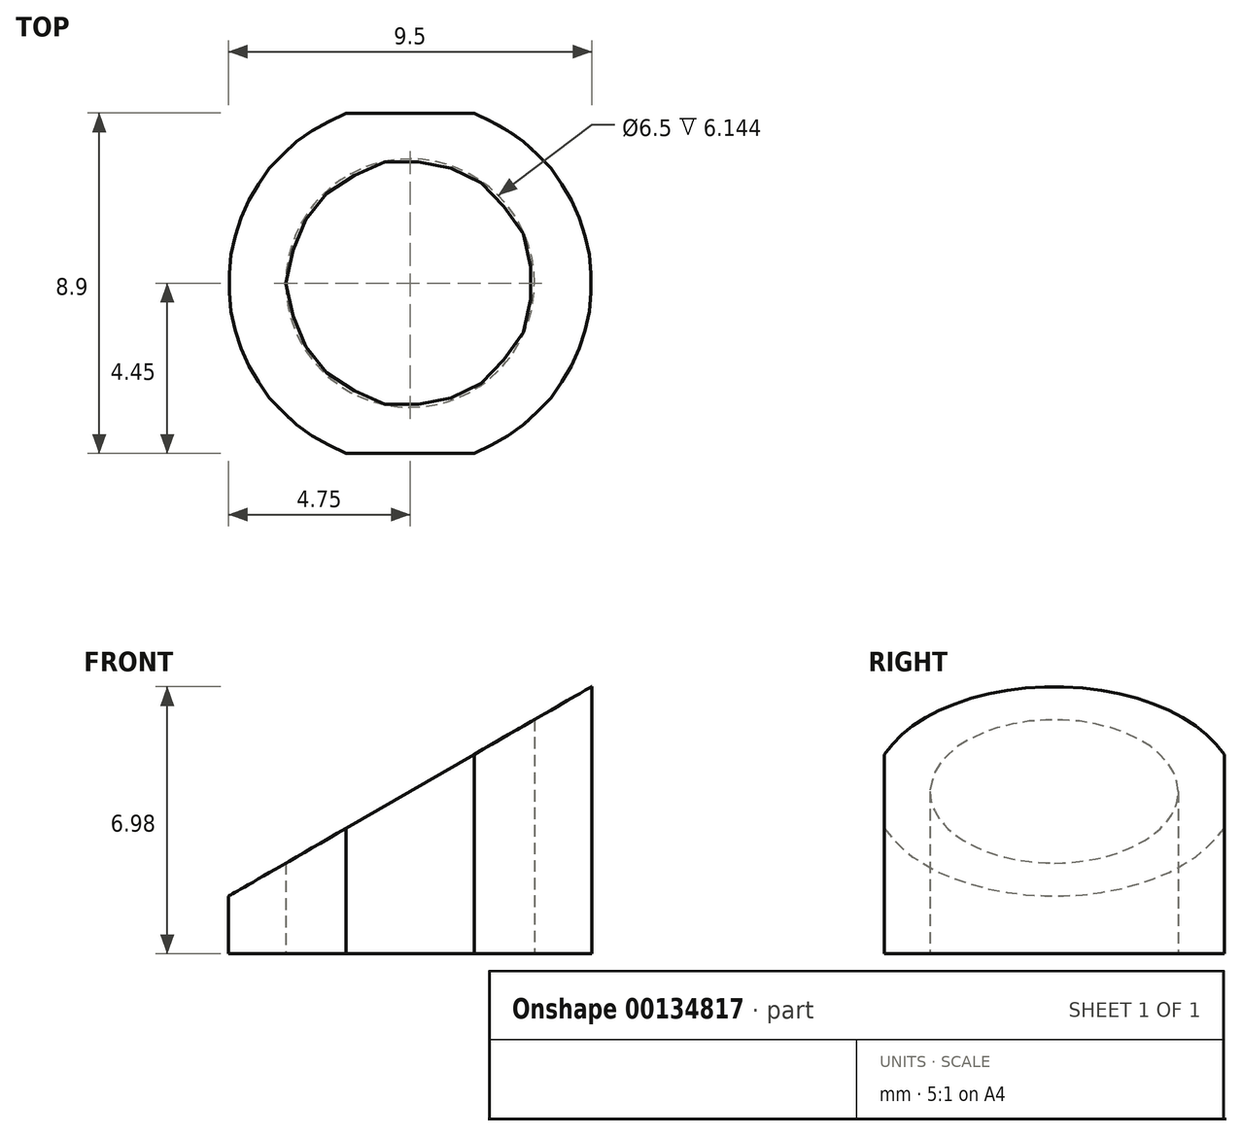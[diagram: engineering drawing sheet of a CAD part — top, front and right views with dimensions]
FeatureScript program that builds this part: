
annotation { "Feature Type Name" : "Feature", "Feature Type Description" : "" }
export const myFeature = defineFeature(function(context is Context, id is Id, definition is map)
    precondition{}
    {
        {
            var Q0;
            Q0=qCreatedBy(makeId("Top.planeOp"),FACE);
            var sketch = newSketch(context, id + "F0", { "sketchPlane" : qUnion([Q0])});
            skCircle(sketch, "E0", {"center": v(0, 0) * mm, "radius": 3.25 * mm});
            skCircle(sketch, "E1", {"center": v(0, 0) * mm, "radius": 4.75 * mm});
            skSolve(sketch);
        }
        {
            var Q0;
            Q0 = qSketchRegion(id + "F0", true);
            extrude(context, id + "F1", {"entities" : qUnion([Q0]), "depth" : 10 * mm});
        }
        {
            var Q0;
            Q0=qCreatedBy(makeId("Front.planeOp"),FACE);
            var sketch = newSketch(context, id + "F2", { "sketchPlane" : qUnion([Q0])});
            skLineSegment(sketch, "E2.0", {"start": v(-4.75, 10) * mm, "end": v(4.75, 10) * mm});
            skLineSegment(sketch, "E3", {"start": v(-4.75, 10) * mm, "end": v(-4.75, 1.5) * mm});
            skLineSegment(sketch, "E4", {"start": v(-4.75, 1.5) * mm, "end": v(4.75, 6.98) * mm});
            skLineSegment(sketch, "E5", {"start": v(4.75, 6.98) * mm, "end": v(4.75, 10) * mm});
            skSolve(sketch);
        }
        {
            var Q0;
            Q0 = qSketchRegion(id + "F2", true);
            extrude(context, id + "F3", {"entities" : qUnion([Q0]), "operationType" : NewBodyOperationType.REMOVE, "endBound" : BoundingType.THROUGH_ALL, "oppositeDirection" : true, "depth" : 25.4 * mm, "hasSecondDirection" : true, "secondDirectionBound" : SecondDirectionBoundingType.THROUGH_ALL, "secondDirectionOppositeDirection" : false, "secondDirectionDepth" : 25.4 * mm});
        }
        {
            var Q0;
            Q0=makeQuery(id+"F1.opExtrude","CAP_FACE",FACE,{"disambiguationData":[OSD([sQuery(id+"F0.wireOp",EDGE,"E0"),sQuery(id+"F0.wireOp",EDGE,"E1")])],"isStart":true});
            var sketch = newSketch(context, id + "F4", { "sketchPlane" : qUnion([Q0])});
            skArc(sketch, "E6.0", {"start": v(1.67, 4.45) * mm, "mid": v(0, 4.75) * mm, "end": v(-1.67, 4.45) * mm});
            skLineSegment(sketch, "E7", {"start": v(-1.67, 4.45) * mm, "end": v(1.67, 4.45) * mm});
            skLineSegment(sketch, "E8", {"start": v(-1.67, -4.45) * mm, "end": v(1.67, -4.45) * mm});
            skArc(sketch, "E9.trimOffspring", {"start": v(-1.67, -4.45) * mm, "mid": v(0, -4.75) * mm, "end": v(1.67, -4.45) * mm});
            skSolve(sketch);
        }
        {
            var Q0;
            Q0 = qSketchRegion(id + "F4", true);
            extrude(context, id + "F5", {"entities" : qUnion([Q0]), "operationType" : NewBodyOperationType.REMOVE, "endBound" : BoundingType.THROUGH_ALL, "oppositeDirection" : true, "depth" : 25.4 * mm});
        }
    });
